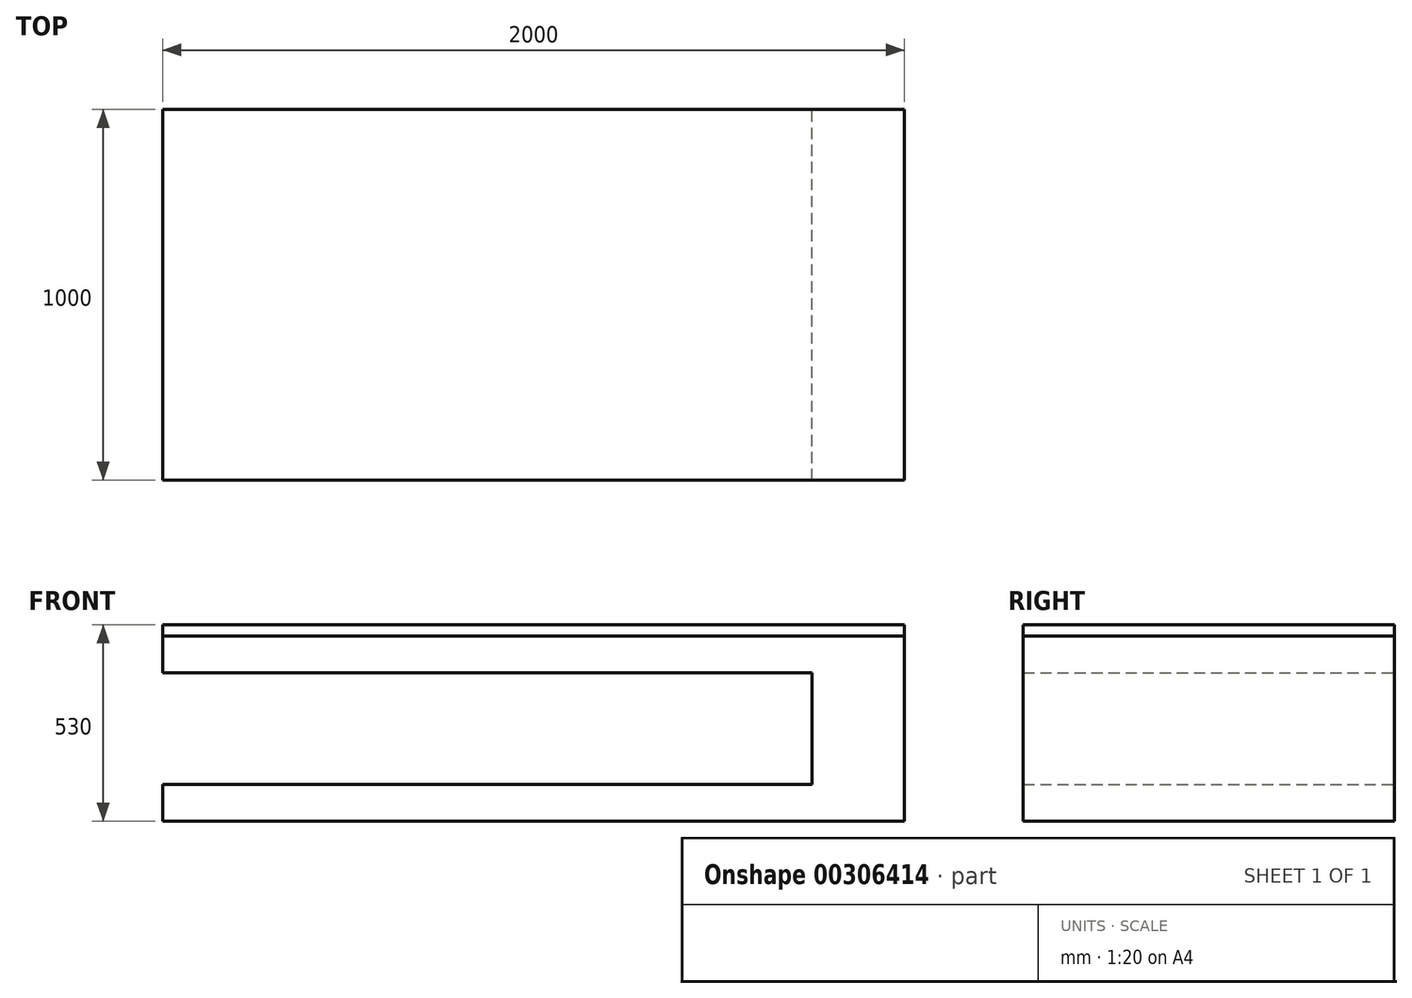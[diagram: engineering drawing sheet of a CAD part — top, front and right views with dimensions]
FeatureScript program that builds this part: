
annotation { "Feature Type Name" : "Feature", "Feature Type Description" : "" }
export const myFeature = defineFeature(function(context is Context, id is Id, definition is map)
    precondition{}
    {
        {
            var Q0;
            Q0=qCreatedBy(makeId("Front.planeOp"),FACE);
            var sketch = newSketch(context, id + "F0", { "sketchPlane" : qUnion([Q0])});
            skLineSegment(sketch, "E0.bottom", {"start": v(0, 0) * mm, "end": v(-2000, 0) * mm});
            skLineSegment(sketch, "E0.top", {"start": v(0, 500) * mm, "end": v(-2000, 500) * mm});
            skLineSegment(sketch, "E0.left", {"start": v(0, 0) * mm, "end": v(0, 500) * mm});
            skLineSegment(sketch, "E0.right", {"start": v(-2000, 0) * mm, "end": v(-2000, 500) * mm});
            skLineSegment(sketch, "E1.bottom", {"start": v(-2000, 400) * mm, "end": v(-250, 400) * mm});
            skLineSegment(sketch, "E1.top", {"start": v(-2000, 100) * mm, "end": v(-250, 100) * mm});
            skLineSegment(sketch, "E1.left", {"start": v(-2000, 400) * mm, "end": v(-2000, 100) * mm});
            skLineSegment(sketch, "E1.right", {"start": v(-250, 400) * mm, "end": v(-250, 100) * mm});
            skSolve(sketch);
        }
        {
            var Q0;
            {var subQ1=sQuery(id+"F0.wireOp",EDGE,"E0.bottom");Q0=makeQuery(id+"F0.imprint","IMPRINT",FACE,{"disambiguationData":[TD([[makeQuery(id+"F0.imprint","IMPRINT",EDGE,{"derivedFrom":subQ1}),-1.0]])]});}
            var Q1;
            Q1 = qSketchRegion(id + "F2", true);
            extrude(context, id + "F1", {"entities" : qUnion([Q0, Q1]), "depth" : 1000 * mm});
        }
        {
            var Q0;
            Q0=makeQuery(id+"F1.opExtrude","CAP_FACE",FACE,{"disambiguationData":[OSD([sQuery(id+"F0.wireOp",EDGE,"E0.bottom"),sQuery(id+"F0.wireOp",EDGE,"E0.top"),sQuery(id+"F0.wireOp",EDGE,"E0.left"),sQuery(id+"F0.wireOp",EDGE,"E0.right"),sQuery(id+"F0.wireOp",EDGE,"E1.bottom"),sQuery(id+"F0.wireOp",EDGE,"E1.top"),sQuery(id+"F0.wireOp",EDGE,"E1.right")])],"isStart":false});
            var sketch = newSketch(context, id + "F2", { "sketchPlane" : qUnion([Q0])});
            skSolve(sketch);
        }
        {
            var Q0;
            {var subQ1=sQuery(id+"F0.wireOp",EDGE,"E0.bottom");Q0=makeQuery(id+"F2.imprint","IMPRINT",FACE,{"disambiguationData":[TD([[makeQuery(id+"F2.imprint","IMPRINT",EDGE,{"derivedFrom":makeQuery(id+"F1.opExtrude","CAP_EDGE",EDGE,{"disambiguationData":[OSD([subQ1])],"isStart":false})}),-1.0]])]});}
            var sketch = newSketch(context, id + "F3", { "sketchPlane" : qUnion([Q0])});
            skLineSegment(sketch, "E2.bottom", {"start": v(-2000, 500) * mm, "end": v(0, 500) * mm});
            skLineSegment(sketch, "E2.top", {"start": v(-2000, 530) * mm, "end": v(0, 530) * mm});
            skLineSegment(sketch, "E2.left", {"start": v(-2000, 500) * mm, "end": v(-2000, 530) * mm});
            skLineSegment(sketch, "E2.right", {"start": v(0, 500) * mm, "end": v(0, 530) * mm});
            skSolve(sketch);
        }
        {
            var Q0;
            Q0=makeQuery(id+"F3.imprint","IMPRINT",FACE,{"disambiguationData":[TD([[makeQuery(id+"F3.imprint","IMPRINT",EDGE,{"derivedFrom":sQuery(id+"F3.wireOp",EDGE,"E2.bottom")}),-1.0]])]});
            extrude(context, id + "F4", {"entities" : qUnion([Q0]), "oppositeDirection" : true, "depth" : 1000 * mm});
        }
    });
